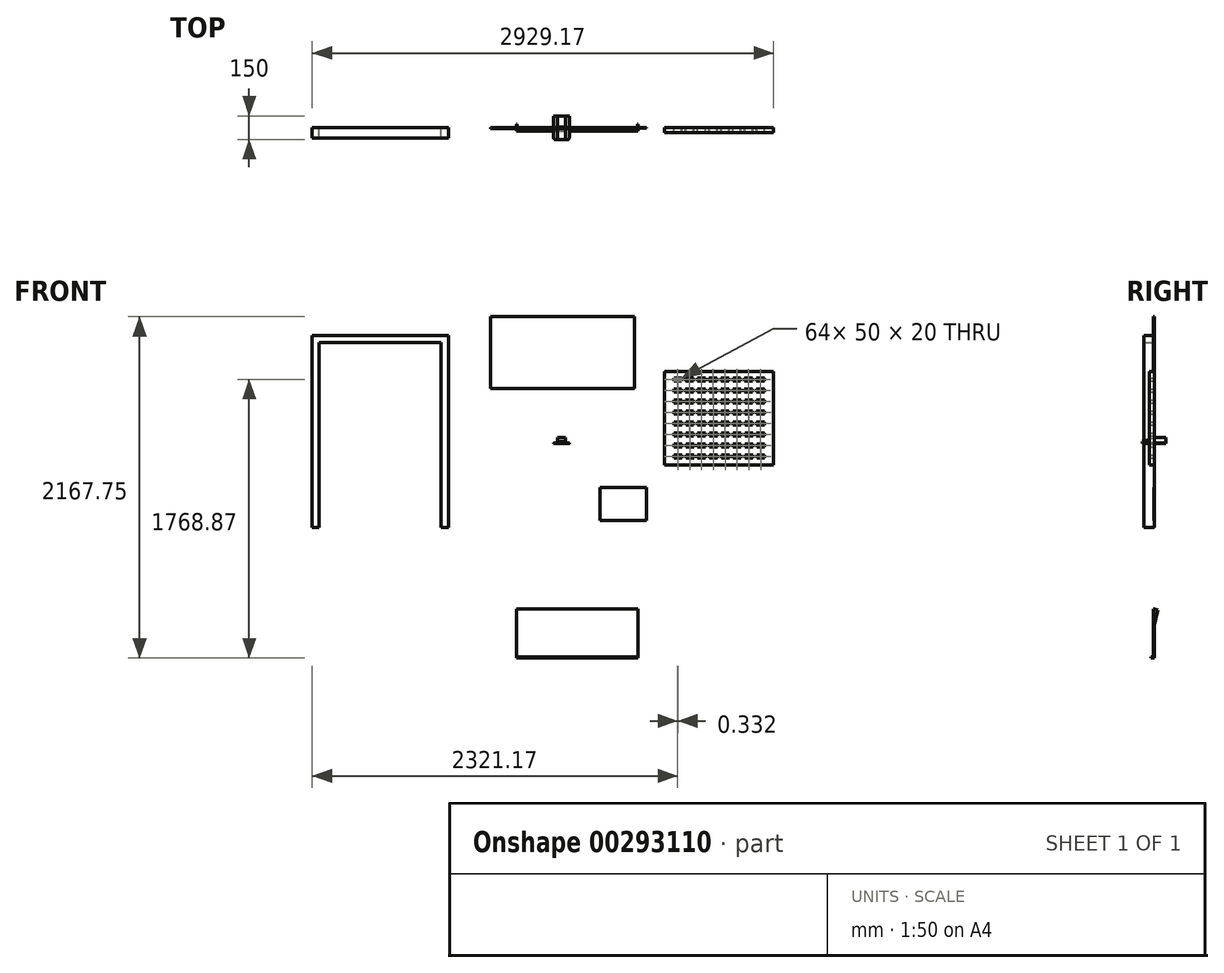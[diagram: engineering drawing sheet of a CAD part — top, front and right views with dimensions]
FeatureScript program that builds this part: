
annotation { "Feature Type Name" : "Feature", "Feature Type Description" : "" }
export const myFeature = defineFeature(function(context is Context, id is Id, definition is map)
    precondition{}
    {
        {
            var Q0;
            Q0=qCreatedBy(makeId("Top.planeOp"),FACE);
            var sketch = newSketch(context, id + "F0", { "sketchPlane" : qUnion([Q0])});
            skLineSegment(sketch, "E0.bottom", {"start": v(-50, 75) * mm, "end": v(50, 75) * mm});
            skLineSegment(sketch, "E0.top", {"start": v(-50, -75) * mm, "end": v(50, -75) * mm});
            skLineSegment(sketch, "E0.left", {"start": v(-50, 75) * mm, "end": v(-50, -75) * mm});
            skLineSegment(sketch, "E0.right", {"start": v(50, 75) * mm, "end": v(50, -75) * mm});
            skPoint(sketch, "E0.middle", {"position": v(0, 0) * mm});
            skSolve(sketch);
        }
        {
            var Q0;
            Q0=makeQuery(id+"F0.imprint","IMPRINT",FACE,{"disambiguationData":[TD([[makeQuery(id+"F0.imprint","IMPRINT",EDGE,{"derivedFrom":sQuery(id+"F0.wireOp",EDGE,"E0.bottom")}),-1.0]])]});
            extrude(context, id + "F1", {"entities" : qUnion([Q0]), "depth" : 3 * mm});
        }
        {
            var Q0;
            Q0=makeQuery(id+"F1.opExtrude","SWEPT_EDGE",EDGE,{"disambiguationData":[OSD([sQuery(id+"F0.wireOp",EDGE,"E0.top"),sQuery(id+"F0.wireOp",EDGE,"E0.left")])]});
            var Q1;
            Q1=makeQuery(id+"F1.opExtrude","SWEPT_EDGE",EDGE,{"disambiguationData":[OSD([sQuery(id+"F0.wireOp",EDGE,"E0.top"),sQuery(id+"F0.wireOp",EDGE,"E0.right")])]});
            fillet(context, id + "F2", {"entities" : qUnion([Q0, Q1]), "radius" : 10 * mm, "tangentPropagation" : true, "allowEdgeOverflow" : false});
        }
        {
            var Q0;
            Q0=makeQuery(id+"F1.opExtrude","CAP_FACE",FACE,{"disambiguationData":[OSD([sQuery(id+"F0.wireOp",EDGE,"E0.bottom"),sQuery(id+"F0.wireOp",EDGE,"E0.top"),sQuery(id+"F0.wireOp",EDGE,"E0.left"),sQuery(id+"F0.wireOp",EDGE,"E0.right")])],"isStart":false});
            var sketch = newSketch(context, id + "F3", { "sketchPlane" : qUnion([Q0])});
            skLineSegment(sketch, "E1.bottom", {"start": v(-25, 75) * mm, "end": v(25, 75) * mm});
            skLineSegment(sketch, "E1.top", {"start": v(-25, -75) * mm, "end": v(25, -75) * mm});
            skLineSegment(sketch, "E1.left", {"start": v(-25, 75) * mm, "end": v(-25, -75) * mm});
            skLineSegment(sketch, "E1.right", {"start": v(25, 75) * mm, "end": v(25, -75) * mm});
            skPoint(sketch, "E1.middle", {"position": v(0, 0) * mm});
            skSolve(sketch);
        }
        {
            var Q0;
            {var subQ0=sQuery(id+"F3.wireOp",EDGE,"E1.bottom");Q0=makeQuery(id+"F3.imprint","IMPRINT",FACE,{"disambiguationData":[TD([[makeQuery(id+"F3.imprint","IMPRINT",EDGE,{"derivedFrom":subQ0}),-1.0]])]});}
            extrude(context, id + "F4", {"entities" : qUnion([Q0]), "operationType" : NewBodyOperationType.ADD, "depth" : 35 * mm});
        }
        {
            var Q0;
            Q0=makeQuery(id+"F4.opExtrude","SWEPT_FACE",FACE,{"disambiguationData":[OSD([sQuery(id+"F3.wireOp",EDGE,"E1.right")])]});
            var sketch = newSketch(context, id + "F5", { "sketchPlane" : qUnion([Q0])});
            skLineSegment(sketch, "E2", {"start": v(5, 3) * mm, "end": v(5, 38) * mm});
            skLineSegment(sketch, "E3", {"start": v(5, 38) * mm, "end": v(-75, 13) * mm});
            skLineSegment(sketch, "E4", {"start": v(-75, 13) * mm, "end": v(-75, 3) * mm});
            skLineSegment(sketch, "E5", {"start": v(-75, 3) * mm, "end": v(5, 3) * mm});
            skSolve(sketch);
        }
        {
            var Q0;
            {var subQ0=sQuery(id+"F5.wireOp",EDGE,"E3");Q0=makeQuery(id+"F5.imprint","IMPRINT",FACE,{"disambiguationData":[TD([[makeQuery(id+"F5.imprint","IMPRINT",EDGE,{"derivedFrom":subQ0}),-1.0]])]});}
            extrude(context, id + "F6", {"entities" : qUnion([Q0]), "operationType" : NewBodyOperationType.REMOVE, "endBound" : BoundingType.THROUGH_ALL, "oppositeDirection" : true, "depth" : 25 * mm});
        }
        {
            var Q0;
            Q0=qCreatedBy(makeId("Front.planeOp"),FACE);
            var sketch = newSketch(context, id + "F7", { "sketchPlane" : qUnion([Q0])});
            skLineSegment(sketch, "E6.bottom", {"start": v(-1582.46, -533.96) * mm, "end": v(-1537.46, -533.96) * mm});
            skLineSegment(sketch, "E6.left", {"start": v(-1582.46, -533.96) * mm, "end": v(-1582.46, 685.04) * mm});
            skLineSegment(sketch, "E6.right", {"start": v(-1537.46, -533.96) * mm, "end": v(-1537.46, 640.04) * mm});
            skLineSegment(sketch, "E7.top", {"start": v(-1537.46, 640.04) * mm, "end": v(-763.06, 640.04) * mm});
            skLineSegment(sketch, "E8.top", {"start": v(-763.06, -533.96) * mm, "end": v(-718.06, -533.96) * mm});
            skLineSegment(sketch, "E8.left", {"start": v(-763.06, 640.04) * mm, "end": v(-763.06, -533.96) * mm});
            skLineSegment(sketch, "E8.right", {"start": v(-718.06, 685.04) * mm, "end": v(-718.06, -533.96) * mm});
            skLineSegment(sketch, "E9", {"start": v(-1582.46, 685.04) * mm, "end": v(-718.06, 685.04) * mm});
            skSolve(sketch);
        }
        {
            var Q0;
            {var subQ0=sQuery(id+"F7.wireOp",EDGE,"E7.bottom");Q0=makeQuery(id+"F7.imprint","IMPRINT",FACE,{"disambiguationData":[TD([[makeQuery(id+"F7.imprint","IMPRINT",EDGE,{"derivedFrom":subQ0}),-1.0]])]});}
            var Q1;
            Q1=makeQuery(id+"F7.imprint","IMPRINT",FACE,{"disambiguationData":[TD([[makeQuery(id+"F7.imprint","IMPRINT",EDGE,{"derivedFrom":sQuery(id+"F7.wireOp",EDGE,"E6.bottom")}),1.0]])]});
            var Q2;
            {var subQ3=sQuery(id+"F7.wireOp",EDGE,"Cl1eL8Ux-WlNg-qc7l-GYTB-HFergLuJIKgZ.bottom");Q2=makeQuery(id+"F7.imprint","IMPRINT",FACE,{"disambiguationData":[TD([[makeQuery(id+"F7.imprint","IMPRINT",EDGE,{"derivedFrom":subQ3}),-1.0]])]});}
            var Q3;
            {var subQ0=sQuery(id+"F7.wireOp",EDGE,"AxVRE3I6-bPMa-kPDy-dnkS-AJJv6BN4a7yn.bottom");Q3=makeQuery(id+"F7.imprint","IMPRINT",FACE,{"disambiguationData":[TD([[makeQuery(id+"F7.imprint","IMPRINT",EDGE,{"derivedFrom":subQ0}),-1.0]])]});}
            var Q4;
            {var subQ3=sQuery(id+"F7.wireOp",EDGE,"E8.bottom");Q4=makeQuery(id+"F7.imprint","IMPRINT",FACE,{"disambiguationData":[TD([[makeQuery(id+"F7.imprint","IMPRINT",EDGE,{"derivedFrom":subQ3}),-1.0]])]});}
            extrude(context, id + "F8", {"entities" : qUnion([Q0, Q1, Q2, Q3, Q4]), "depth" : 65 * mm});
        }
        {
            var Q0;
            Q0=qCreatedBy(makeId("Front.planeOp"),FACE);
            var sketch = newSketch(context, id + "F9", { "sketchPlane" : qUnion([Q0])});
            skLineSegment(sketch, "E10.bottom", {"start": v(653.71, 457) * mm, "end": v(1346.71, 457) * mm});
            skLineSegment(sketch, "E10.top", {"start": v(653.71, -136) * mm, "end": v(1346.71, -136) * mm});
            skLineSegment(sketch, "E10.left", {"start": v(653.71, 457) * mm, "end": v(653.71, -136) * mm});
            skLineSegment(sketch, "E10.right", {"start": v(1346.71, 457) * mm, "end": v(1346.71, -136) * mm});
            skLineSegment(sketch, "E11.bottom", {"start": v(713.71, 417) * mm, "end": v(763.71, 417) * mm});
            skLineSegment(sketch, "E11.top", {"start": v(713.71, 397) * mm, "end": v(763.71, 397) * mm});
            skLineSegment(sketch, "E11.left", {"start": v(713.71, 417) * mm, "end": v(713.71, 397) * mm});
            skLineSegment(sketch, "E11.right", {"start": v(763.71, 417) * mm, "end": v(763.71, 397) * mm});
            skLineSegment(sketch, "E12.0.1.0", {"start": v(714.04, 347) * mm, "end": v(764.04, 347) * mm});
            skLineSegment(sketch, "E12.0.1.1", {"start": v(714.04, 327) * mm, "end": v(764.04, 327) * mm});
            skLineSegment(sketch, "E12.0.1.2", {"start": v(714.04, 347) * mm, "end": v(714.04, 327) * mm});
            skLineSegment(sketch, "E12.0.2.0", {"start": v(714.37, 277) * mm, "end": v(764.37, 277) * mm});
            skLineSegment(sketch, "E12.0.2.1", {"start": v(714.37, 257) * mm, "end": v(764.37, 257) * mm});
            skLineSegment(sketch, "E12.0.2.2", {"start": v(714.37, 277) * mm, "end": v(714.37, 257) * mm});
            skLineSegment(sketch, "E12.0.3.0", {"start": v(714.7, 207) * mm, "end": v(764.7, 207) * mm});
            skLineSegment(sketch, "E12.0.3.1", {"start": v(714.7, 187) * mm, "end": v(764.7, 187) * mm});
            skLineSegment(sketch, "E12.0.3.2", {"start": v(714.7, 207) * mm, "end": v(714.7, 187) * mm});
            skLineSegment(sketch, "E12.0.4.0", {"start": v(715.04, 137) * mm, "end": v(765.04, 137) * mm});
            skLineSegment(sketch, "E12.0.4.1", {"start": v(715.04, 117) * mm, "end": v(765.04, 117) * mm});
            skLineSegment(sketch, "E12.0.4.2", {"start": v(715.04, 137) * mm, "end": v(715.04, 117) * mm});
            skLineSegment(sketch, "E12.0.5.0", {"start": v(715.37, 67) * mm, "end": v(765.37, 67) * mm});
            skLineSegment(sketch, "E12.0.5.1", {"start": v(715.37, 47) * mm, "end": v(765.37, 47) * mm});
            skLineSegment(sketch, "E12.0.5.2", {"start": v(715.37, 67) * mm, "end": v(715.37, 47) * mm});
            skLineSegment(sketch, "E12.0.6.0", {"start": v(715.7, -3) * mm, "end": v(765.7, -3) * mm});
            skLineSegment(sketch, "E12.0.6.1", {"start": v(715.7, -23) * mm, "end": v(765.7, -23) * mm});
            skLineSegment(sketch, "E12.0.6.2", {"start": v(715.7, -3) * mm, "end": v(715.7, -23) * mm});
            skLineSegment(sketch, "E12.1.0.0", {"start": v(788.71, 417) * mm, "end": v(838.71, 417) * mm});
            skLineSegment(sketch, "E12.1.0.1", {"start": v(788.71, 397) * mm, "end": v(838.71, 397) * mm});
            skLineSegment(sketch, "E12.1.0.2", {"start": v(788.71, 417) * mm, "end": v(788.71, 397) * mm});
            skLineSegment(sketch, "E12.1.1.0", {"start": v(789.04, 347) * mm, "end": v(839.04, 347) * mm});
            skLineSegment(sketch, "E12.1.1.1", {"start": v(789.04, 327) * mm, "end": v(839.04, 327) * mm});
            skLineSegment(sketch, "E12.1.1.2", {"start": v(789.04, 347) * mm, "end": v(789.04, 327) * mm});
            skLineSegment(sketch, "E12.1.2.0", {"start": v(789.37, 277) * mm, "end": v(839.37, 277) * mm});
            skLineSegment(sketch, "E12.1.2.1", {"start": v(789.37, 257) * mm, "end": v(839.37, 257) * mm});
            skLineSegment(sketch, "E12.1.2.2", {"start": v(789.37, 277) * mm, "end": v(789.37, 257) * mm});
            skLineSegment(sketch, "E12.1.3.0", {"start": v(789.7, 207) * mm, "end": v(839.7, 207) * mm});
            skLineSegment(sketch, "E12.1.3.1", {"start": v(789.7, 187) * mm, "end": v(839.7, 187) * mm});
            skLineSegment(sketch, "E12.1.3.2", {"start": v(789.7, 207) * mm, "end": v(789.7, 187) * mm});
            skLineSegment(sketch, "E12.1.4.0", {"start": v(790.04, 137) * mm, "end": v(840.04, 137) * mm});
            skLineSegment(sketch, "E12.1.4.1", {"start": v(790.04, 117) * mm, "end": v(840.04, 117) * mm});
            skLineSegment(sketch, "E12.1.4.2", {"start": v(790.04, 137) * mm, "end": v(790.04, 117) * mm});
            skLineSegment(sketch, "E12.1.5.0", {"start": v(790.37, 67) * mm, "end": v(840.37, 67) * mm});
            skLineSegment(sketch, "E12.1.5.1", {"start": v(790.37, 47) * mm, "end": v(840.37, 47) * mm});
            skLineSegment(sketch, "E12.1.5.2", {"start": v(790.37, 67) * mm, "end": v(790.37, 47) * mm});
            skLineSegment(sketch, "E12.1.6.0", {"start": v(790.7, -3) * mm, "end": v(840.7, -3) * mm});
            skLineSegment(sketch, "E12.1.6.1", {"start": v(790.7, -23) * mm, "end": v(840.7, -23) * mm});
            skLineSegment(sketch, "E12.1.6.2", {"start": v(790.7, -3) * mm, "end": v(790.7, -23) * mm});
            skLineSegment(sketch, "E12.2.0.0", {"start": v(863.71, 417) * mm, "end": v(913.71, 417) * mm});
            skLineSegment(sketch, "E12.2.0.1", {"start": v(863.71, 397) * mm, "end": v(913.71, 397) * mm});
            skLineSegment(sketch, "E12.2.0.2", {"start": v(863.71, 417) * mm, "end": v(863.71, 397) * mm});
            skLineSegment(sketch, "E12.2.1.0", {"start": v(864.04, 347) * mm, "end": v(914.04, 347) * mm});
            skLineSegment(sketch, "E12.2.1.1", {"start": v(864.04, 327) * mm, "end": v(914.04, 327) * mm});
            skLineSegment(sketch, "E12.2.1.2", {"start": v(864.04, 347) * mm, "end": v(864.04, 327) * mm});
            skLineSegment(sketch, "E12.2.2.0", {"start": v(864.37, 277) * mm, "end": v(914.37, 277) * mm});
            skLineSegment(sketch, "E12.2.2.1", {"start": v(864.37, 257) * mm, "end": v(914.37, 257) * mm});
            skLineSegment(sketch, "E12.2.2.2", {"start": v(864.37, 277) * mm, "end": v(864.37, 257) * mm});
            skLineSegment(sketch, "E12.2.3.0", {"start": v(864.7, 207) * mm, "end": v(914.7, 207) * mm});
            skLineSegment(sketch, "E12.2.3.1", {"start": v(864.7, 187) * mm, "end": v(914.7, 187) * mm});
            skLineSegment(sketch, "E12.2.3.2", {"start": v(864.7, 207) * mm, "end": v(864.7, 187) * mm});
            skLineSegment(sketch, "E12.2.4.0", {"start": v(865.04, 137) * mm, "end": v(915.04, 137) * mm});
            skLineSegment(sketch, "E12.2.4.1", {"start": v(865.04, 117) * mm, "end": v(915.04, 117) * mm});
            skLineSegment(sketch, "E12.2.4.2", {"start": v(865.04, 137) * mm, "end": v(865.04, 117) * mm});
            skLineSegment(sketch, "E12.2.5.0", {"start": v(865.37, 67) * mm, "end": v(915.37, 67) * mm});
            skLineSegment(sketch, "E12.2.5.1", {"start": v(865.37, 47) * mm, "end": v(915.37, 47) * mm});
            skLineSegment(sketch, "E12.2.5.2", {"start": v(865.37, 67) * mm, "end": v(865.37, 47) * mm});
            skLineSegment(sketch, "E12.2.6.0", {"start": v(865.7, -3) * mm, "end": v(915.7, -3) * mm});
            skLineSegment(sketch, "E12.2.6.1", {"start": v(865.7, -23) * mm, "end": v(915.7, -23) * mm});
            skLineSegment(sketch, "E12.2.6.2", {"start": v(865.7, -3) * mm, "end": v(865.7, -23) * mm});
            skLineSegment(sketch, "E12.3.0.0", {"start": v(938.71, 417) * mm, "end": v(988.71, 417) * mm});
            skLineSegment(sketch, "E12.3.0.1", {"start": v(938.71, 397) * mm, "end": v(988.71, 397) * mm});
            skLineSegment(sketch, "E12.3.0.2", {"start": v(938.71, 417) * mm, "end": v(938.71, 397) * mm});
            skLineSegment(sketch, "E12.3.1.0", {"start": v(939.04, 347) * mm, "end": v(989.04, 347) * mm});
            skLineSegment(sketch, "E12.3.1.1", {"start": v(939.04, 327) * mm, "end": v(989.04, 327) * mm});
            skLineSegment(sketch, "E12.3.1.2", {"start": v(939.04, 347) * mm, "end": v(939.04, 327) * mm});
            skLineSegment(sketch, "E12.3.2.0", {"start": v(939.37, 277) * mm, "end": v(989.37, 277) * mm});
            skLineSegment(sketch, "E12.3.2.1", {"start": v(939.37, 257) * mm, "end": v(989.37, 257) * mm});
            skLineSegment(sketch, "E12.3.2.2", {"start": v(939.37, 277) * mm, "end": v(939.37, 257) * mm});
            skLineSegment(sketch, "E12.3.3.0", {"start": v(939.7, 207) * mm, "end": v(989.7, 207) * mm});
            skLineSegment(sketch, "E12.3.3.1", {"start": v(939.7, 187) * mm, "end": v(989.7, 187) * mm});
            skLineSegment(sketch, "E12.3.3.2", {"start": v(939.7, 207) * mm, "end": v(939.7, 187) * mm});
            skLineSegment(sketch, "E12.3.4.0", {"start": v(940.04, 137) * mm, "end": v(990.04, 137) * mm});
            skLineSegment(sketch, "E12.3.4.1", {"start": v(940.04, 117) * mm, "end": v(990.04, 117) * mm});
            skLineSegment(sketch, "E12.3.4.2", {"start": v(940.04, 137) * mm, "end": v(940.04, 117) * mm});
            skLineSegment(sketch, "E12.3.5.0", {"start": v(940.37, 67) * mm, "end": v(990.37, 67) * mm});
            skLineSegment(sketch, "E12.3.5.1", {"start": v(940.37, 47) * mm, "end": v(990.37, 47) * mm});
            skLineSegment(sketch, "E12.3.5.2", {"start": v(940.37, 67) * mm, "end": v(940.37, 47) * mm});
            skLineSegment(sketch, "E12.3.6.0", {"start": v(940.7, -3) * mm, "end": v(990.7, -3) * mm});
            skLineSegment(sketch, "E12.3.6.1", {"start": v(940.7, -23) * mm, "end": v(990.7, -23) * mm});
            skLineSegment(sketch, "E12.3.6.2", {"start": v(940.7, -3) * mm, "end": v(940.7, -23) * mm});
            skLineSegment(sketch, "E12.4.0.0", {"start": v(1013.71, 417) * mm, "end": v(1063.71, 417) * mm});
            skLineSegment(sketch, "E12.4.0.1", {"start": v(1013.71, 397) * mm, "end": v(1063.71, 397) * mm});
            skLineSegment(sketch, "E12.4.0.2", {"start": v(1013.71, 417) * mm, "end": v(1013.71, 397) * mm});
            skLineSegment(sketch, "E12.4.1.0", {"start": v(1014.04, 347) * mm, "end": v(1064.04, 347) * mm});
            skLineSegment(sketch, "E12.4.1.1", {"start": v(1014.04, 327) * mm, "end": v(1064.04, 327) * mm});
            skLineSegment(sketch, "E12.4.1.2", {"start": v(1014.04, 347) * mm, "end": v(1014.04, 327) * mm});
            skLineSegment(sketch, "E12.4.2.0", {"start": v(1014.37, 277) * mm, "end": v(1064.37, 277) * mm});
            skLineSegment(sketch, "E12.4.2.1", {"start": v(1014.37, 257) * mm, "end": v(1064.37, 257) * mm});
            skLineSegment(sketch, "E12.4.2.2", {"start": v(1014.37, 277) * mm, "end": v(1014.37, 257) * mm});
            skLineSegment(sketch, "E12.4.3.0", {"start": v(1014.7, 207) * mm, "end": v(1064.7, 207) * mm});
            skLineSegment(sketch, "E12.4.3.1", {"start": v(1014.7, 187) * mm, "end": v(1064.7, 187) * mm});
            skLineSegment(sketch, "E12.4.3.2", {"start": v(1014.7, 207) * mm, "end": v(1014.7, 187) * mm});
            skLineSegment(sketch, "E12.4.4.0", {"start": v(1015.04, 137) * mm, "end": v(1065.04, 137) * mm});
            skLineSegment(sketch, "E12.4.4.1", {"start": v(1015.04, 117) * mm, "end": v(1065.04, 117) * mm});
            skLineSegment(sketch, "E12.4.4.2", {"start": v(1015.04, 137) * mm, "end": v(1015.04, 117) * mm});
            skLineSegment(sketch, "E12.4.5.0", {"start": v(1015.37, 67) * mm, "end": v(1065.37, 67) * mm});
            skLineSegment(sketch, "E12.4.5.1", {"start": v(1015.37, 47) * mm, "end": v(1065.37, 47) * mm});
            skLineSegment(sketch, "E12.4.5.2", {"start": v(1015.37, 67) * mm, "end": v(1015.37, 47) * mm});
            skLineSegment(sketch, "E12.4.6.0", {"start": v(1015.7, -3) * mm, "end": v(1065.7, -3) * mm});
            skLineSegment(sketch, "E12.4.6.1", {"start": v(1015.7, -23) * mm, "end": v(1065.7, -23) * mm});
            skLineSegment(sketch, "E12.4.6.2", {"start": v(1015.7, -3) * mm, "end": v(1015.7, -23) * mm});
            skLineSegment(sketch, "E12.5.0.0", {"start": v(1088.71, 417) * mm, "end": v(1138.71, 417) * mm});
            skLineSegment(sketch, "E12.5.0.1", {"start": v(1088.71, 397) * mm, "end": v(1138.71, 397) * mm});
            skLineSegment(sketch, "E12.5.0.2", {"start": v(1088.71, 417) * mm, "end": v(1088.71, 397) * mm});
            skLineSegment(sketch, "E12.5.1.0", {"start": v(1089.04, 347) * mm, "end": v(1139.04, 347) * mm});
            skLineSegment(sketch, "E12.5.1.1", {"start": v(1089.04, 327) * mm, "end": v(1139.04, 327) * mm});
            skLineSegment(sketch, "E12.5.1.2", {"start": v(1089.04, 347) * mm, "end": v(1089.04, 327) * mm});
            skLineSegment(sketch, "E12.5.2.0", {"start": v(1089.37, 277) * mm, "end": v(1139.37, 277) * mm});
            skLineSegment(sketch, "E12.5.2.1", {"start": v(1089.37, 257) * mm, "end": v(1139.37, 257) * mm});
            skLineSegment(sketch, "E12.5.2.2", {"start": v(1089.37, 277) * mm, "end": v(1089.37, 257) * mm});
            skLineSegment(sketch, "E12.5.3.0", {"start": v(1089.7, 207) * mm, "end": v(1139.7, 207) * mm});
            skLineSegment(sketch, "E12.5.3.1", {"start": v(1089.7, 187) * mm, "end": v(1139.7, 187) * mm});
            skLineSegment(sketch, "E12.5.3.2", {"start": v(1089.7, 207) * mm, "end": v(1089.7, 187) * mm});
            skLineSegment(sketch, "E12.5.4.0", {"start": v(1090.04, 137) * mm, "end": v(1140.04, 137) * mm});
            skLineSegment(sketch, "E12.5.4.1", {"start": v(1090.04, 117) * mm, "end": v(1140.04, 117) * mm});
            skLineSegment(sketch, "E12.5.4.2", {"start": v(1090.04, 137) * mm, "end": v(1090.04, 117) * mm});
            skLineSegment(sketch, "E12.5.5.0", {"start": v(1090.37, 67) * mm, "end": v(1140.37, 67) * mm});
            skLineSegment(sketch, "E12.5.5.1", {"start": v(1090.37, 47) * mm, "end": v(1140.37, 47) * mm});
            skLineSegment(sketch, "E12.5.5.2", {"start": v(1090.37, 67) * mm, "end": v(1090.37, 47) * mm});
            skLineSegment(sketch, "E12.5.6.0", {"start": v(1090.7, -3) * mm, "end": v(1140.7, -3) * mm});
            skLineSegment(sketch, "E12.5.6.1", {"start": v(1090.7, -23) * mm, "end": v(1140.7, -23) * mm});
            skLineSegment(sketch, "E12.5.6.2", {"start": v(1090.7, -3) * mm, "end": v(1090.7, -23) * mm});
            skLineSegment(sketch, "E12.6.0.0", {"start": v(1163.71, 417) * mm, "end": v(1213.71, 417) * mm});
            skLineSegment(sketch, "E12.6.0.1", {"start": v(1163.71, 397) * mm, "end": v(1213.71, 397) * mm});
            skLineSegment(sketch, "E12.6.0.2", {"start": v(1163.71, 417) * mm, "end": v(1163.71, 397) * mm});
            skLineSegment(sketch, "E12.6.1.0", {"start": v(1164.04, 347) * mm, "end": v(1214.04, 347) * mm});
            skLineSegment(sketch, "E12.6.1.1", {"start": v(1164.04, 327) * mm, "end": v(1214.04, 327) * mm});
            skLineSegment(sketch, "E12.6.1.2", {"start": v(1164.04, 347) * mm, "end": v(1164.04, 327) * mm});
            skLineSegment(sketch, "E12.6.2.0", {"start": v(1164.37, 277) * mm, "end": v(1214.37, 277) * mm});
            skLineSegment(sketch, "E12.6.2.1", {"start": v(1164.37, 257) * mm, "end": v(1214.37, 257) * mm});
            skLineSegment(sketch, "E12.6.2.2", {"start": v(1164.37, 277) * mm, "end": v(1164.37, 257) * mm});
            skLineSegment(sketch, "E12.6.3.0", {"start": v(1164.7, 207) * mm, "end": v(1214.7, 207) * mm});
            skLineSegment(sketch, "E12.6.3.1", {"start": v(1164.7, 187) * mm, "end": v(1214.7, 187) * mm});
            skLineSegment(sketch, "E12.6.3.2", {"start": v(1164.7, 207) * mm, "end": v(1164.7, 187) * mm});
            skLineSegment(sketch, "E12.6.4.0", {"start": v(1165.04, 137) * mm, "end": v(1215.04, 137) * mm});
            skLineSegment(sketch, "E12.6.4.1", {"start": v(1165.04, 117) * mm, "end": v(1215.04, 117) * mm});
            skLineSegment(sketch, "E12.6.4.2", {"start": v(1165.04, 137) * mm, "end": v(1165.04, 117) * mm});
            skLineSegment(sketch, "E12.6.5.0", {"start": v(1165.37, 67) * mm, "end": v(1215.37, 67) * mm});
            skLineSegment(sketch, "E12.6.5.1", {"start": v(1165.37, 47) * mm, "end": v(1215.37, 47) * mm});
            skLineSegment(sketch, "E12.6.5.2", {"start": v(1165.37, 67) * mm, "end": v(1165.37, 47) * mm});
            skLineSegment(sketch, "E12.6.6.0", {"start": v(1165.7, -3) * mm, "end": v(1215.7, -3) * mm});
            skLineSegment(sketch, "E12.6.6.1", {"start": v(1165.7, -23) * mm, "end": v(1215.7, -23) * mm});
            skLineSegment(sketch, "E12.6.6.2", {"start": v(1165.7, -3) * mm, "end": v(1165.7, -23) * mm});
            skLineSegment(sketch, "E12.7.0.0", {"start": v(1238.71, 417) * mm, "end": v(1288.71, 417) * mm});
            skLineSegment(sketch, "E12.7.0.1", {"start": v(1238.71, 397) * mm, "end": v(1288.71, 397) * mm});
            skLineSegment(sketch, "E12.7.0.2", {"start": v(1238.71, 417) * mm, "end": v(1238.71, 397) * mm});
            skLineSegment(sketch, "E12.7.1.0", {"start": v(1239.04, 347) * mm, "end": v(1289.04, 347) * mm});
            skLineSegment(sketch, "E12.7.1.1", {"start": v(1239.04, 327) * mm, "end": v(1289.04, 327) * mm});
            skLineSegment(sketch, "E12.7.1.2", {"start": v(1239.04, 347) * mm, "end": v(1239.04, 327) * mm});
            skLineSegment(sketch, "E12.7.2.0", {"start": v(1239.37, 277) * mm, "end": v(1289.37, 277) * mm});
            skLineSegment(sketch, "E12.7.2.1", {"start": v(1239.37, 257) * mm, "end": v(1289.37, 257) * mm});
            skLineSegment(sketch, "E12.7.2.2", {"start": v(1239.37, 277) * mm, "end": v(1239.37, 257) * mm});
            skLineSegment(sketch, "E12.7.3.0", {"start": v(1239.7, 207) * mm, "end": v(1289.7, 207) * mm});
            skLineSegment(sketch, "E12.7.3.1", {"start": v(1239.7, 187) * mm, "end": v(1289.7, 187) * mm});
            skLineSegment(sketch, "E12.7.3.2", {"start": v(1239.7, 207) * mm, "end": v(1239.7, 187) * mm});
            skLineSegment(sketch, "E12.7.4.0", {"start": v(1240.04, 137) * mm, "end": v(1290.04, 137) * mm});
            skLineSegment(sketch, "E12.7.4.1", {"start": v(1240.04, 117) * mm, "end": v(1290.04, 117) * mm});
            skLineSegment(sketch, "E12.7.4.2", {"start": v(1240.04, 137) * mm, "end": v(1240.04, 117) * mm});
            skLineSegment(sketch, "E12.7.5.0", {"start": v(1240.37, 67) * mm, "end": v(1290.37, 67) * mm});
            skLineSegment(sketch, "E12.7.5.1", {"start": v(1240.37, 47) * mm, "end": v(1290.37, 47) * mm});
            skLineSegment(sketch, "E12.7.5.2", {"start": v(1240.37, 67) * mm, "end": v(1240.37, 47) * mm});
            skLineSegment(sketch, "E12.7.6.0", {"start": v(1240.7, -3) * mm, "end": v(1290.7, -3) * mm});
            skLineSegment(sketch, "E12.7.6.1", {"start": v(1240.7, -23) * mm, "end": v(1290.7, -23) * mm});
            skLineSegment(sketch, "E12.7.6.2", {"start": v(1240.7, -3) * mm, "end": v(1240.7, -23) * mm});
            skLineSegment(sketch, "E12.direction1", {"start": v(713.71, 417) * mm, "end": v(788.71, 417) * mm, "construction": true});
            skLineSegment(sketch, "E12.direction2", {"start": v(713.71, 417) * mm, "end": v(714.04, 347) * mm, "construction": true});
            skLineSegment(sketch, "E13.0.0.7", {"start": v(716.03, -73) * mm, "end": v(766.03, -73) * mm});
            skLineSegment(sketch, "E13.3.0.7", {"start": v(716.03, -93) * mm, "end": v(766.03, -93) * mm});
            skLineSegment(sketch, "E13.6.0.7", {"start": v(716.03, -73) * mm, "end": v(716.03, -93) * mm});
            skLineSegment(sketch, "E13.0.1.7", {"start": v(791.03, -73) * mm, "end": v(841.03, -73) * mm});
            skLineSegment(sketch, "E13.3.1.7", {"start": v(791.03, -93) * mm, "end": v(841.03, -93) * mm});
            skLineSegment(sketch, "E13.6.1.7", {"start": v(791.03, -73) * mm, "end": v(791.03, -93) * mm});
            skLineSegment(sketch, "E13.0.2.7", {"start": v(866.03, -73) * mm, "end": v(916.03, -73) * mm});
            skLineSegment(sketch, "E13.3.2.7", {"start": v(866.03, -93) * mm, "end": v(916.03, -93) * mm});
            skLineSegment(sketch, "E13.6.2.7", {"start": v(866.03, -73) * mm, "end": v(866.03, -93) * mm});
            skLineSegment(sketch, "E13.0.3.7", {"start": v(941.03, -73) * mm, "end": v(991.03, -73) * mm});
            skLineSegment(sketch, "E13.3.3.7", {"start": v(941.03, -93) * mm, "end": v(991.03, -93) * mm});
            skLineSegment(sketch, "E13.6.3.7", {"start": v(941.03, -73) * mm, "end": v(941.03, -93) * mm});
            skLineSegment(sketch, "E13.0.4.7", {"start": v(1016.03, -73) * mm, "end": v(1066.03, -73) * mm});
            skLineSegment(sketch, "E13.3.4.7", {"start": v(1016.03, -93) * mm, "end": v(1066.03, -93) * mm});
            skLineSegment(sketch, "E13.6.4.7", {"start": v(1016.03, -73) * mm, "end": v(1016.03, -93) * mm});
            skLineSegment(sketch, "E13.0.5.7", {"start": v(1091.03, -73) * mm, "end": v(1141.03, -73) * mm});
            skLineSegment(sketch, "E13.3.5.7", {"start": v(1091.03, -93) * mm, "end": v(1141.03, -93) * mm});
            skLineSegment(sketch, "E13.6.5.7", {"start": v(1091.03, -73) * mm, "end": v(1091.03, -93) * mm});
            skLineSegment(sketch, "E13.0.6.7", {"start": v(1166.03, -73) * mm, "end": v(1216.03, -73) * mm});
            skLineSegment(sketch, "E13.3.6.7", {"start": v(1166.03, -93) * mm, "end": v(1216.03, -93) * mm});
            skLineSegment(sketch, "E13.6.6.7", {"start": v(1166.03, -73) * mm, "end": v(1166.03, -93) * mm});
            skLineSegment(sketch, "E13.0.7.7", {"start": v(1241.03, -73) * mm, "end": v(1291.03, -73) * mm});
            skLineSegment(sketch, "E13.3.7.7", {"start": v(1241.03, -93) * mm, "end": v(1291.03, -93) * mm});
            skLineSegment(sketch, "E13.6.7.7", {"start": v(1241.03, -73) * mm, "end": v(1241.03, -93) * mm});
            skLineSegment(sketch, "E14", {"start": v(838.71, 417) * mm, "end": v(838.71, 397) * mm});
            skLineSegment(sketch, "E15", {"start": v(913.71, 417) * mm, "end": v(913.71, 397) * mm});
            skLineSegment(sketch, "E16", {"start": v(988.71, 417) * mm, "end": v(988.71, 397) * mm});
            skLineSegment(sketch, "E17", {"start": v(1063.71, 417) * mm, "end": v(1063.71, 397) * mm});
            skLineSegment(sketch, "E18", {"start": v(1138.71, 417) * mm, "end": v(1138.71, 397) * mm});
            skLineSegment(sketch, "E19", {"start": v(1213.71, 417) * mm, "end": v(1213.71, 397) * mm});
            skLineSegment(sketch, "E20", {"start": v(1288.71, 417) * mm, "end": v(1288.71, 397) * mm});
            skLineSegment(sketch, "E21", {"start": v(1289.04, 347) * mm, "end": v(1289.04, 327) * mm});
            skLineSegment(sketch, "E22", {"start": v(1214.04, 347) * mm, "end": v(1214.04, 327) * mm});
            skLineSegment(sketch, "E23", {"start": v(1139.04, 347) * mm, "end": v(1139.04, 327) * mm});
            skLineSegment(sketch, "E24", {"start": v(1064.04, 347) * mm, "end": v(1064.04, 327) * mm});
            skLineSegment(sketch, "E25", {"start": v(989.04, 347) * mm, "end": v(989.04, 327) * mm});
            skLineSegment(sketch, "E26", {"start": v(914.04, 347) * mm, "end": v(914.04, 327) * mm});
            skLineSegment(sketch, "E27", {"start": v(839.04, 347) * mm, "end": v(839.04, 327) * mm});
            skLineSegment(sketch, "E28", {"start": v(764.04, 347) * mm, "end": v(764.04, 327) * mm});
            skLineSegment(sketch, "E29", {"start": v(764.37, 277) * mm, "end": v(764.37, 257) * mm});
            skLineSegment(sketch, "E30", {"start": v(839.37, 277) * mm, "end": v(839.37, 257) * mm});
            skLineSegment(sketch, "E31", {"start": v(914.37, 277) * mm, "end": v(914.37, 257) * mm});
            skLineSegment(sketch, "E32", {"start": v(989.37, 277) * mm, "end": v(989.37, 257) * mm});
            skLineSegment(sketch, "E33", {"start": v(1064.37, 277) * mm, "end": v(1064.37, 257) * mm});
            skLineSegment(sketch, "E34", {"start": v(1139.37, 277) * mm, "end": v(1139.37, 257) * mm});
            skLineSegment(sketch, "E35", {"start": v(1214.37, 277) * mm, "end": v(1214.37, 257) * mm});
            skLineSegment(sketch, "E36", {"start": v(1289.37, 277) * mm, "end": v(1289.37, 257) * mm});
            skLineSegment(sketch, "E37", {"start": v(1289.7, 207) * mm, "end": v(1289.7, 187) * mm});
            skLineSegment(sketch, "E38", {"start": v(1214.7, 207) * mm, "end": v(1214.7, 187) * mm});
            skLineSegment(sketch, "E39", {"start": v(1139.7, 207) * mm, "end": v(1139.7, 187) * mm});
            skLineSegment(sketch, "E40", {"start": v(1064.7, 207) * mm, "end": v(1064.7, 187) * mm});
            skLineSegment(sketch, "E41", {"start": v(989.7, 207) * mm, "end": v(989.7, 187) * mm});
            skLineSegment(sketch, "E42", {"start": v(914.7, 207) * mm, "end": v(914.7, 187) * mm});
            skLineSegment(sketch, "E43", {"start": v(839.7, 207) * mm, "end": v(839.7, 187) * mm});
            skLineSegment(sketch, "E44", {"start": v(764.7, 207) * mm, "end": v(764.7, 187) * mm});
            skLineSegment(sketch, "E45", {"start": v(765.04, 137) * mm, "end": v(765.04, 117) * mm});
            skLineSegment(sketch, "E46", {"start": v(840.04, 137) * mm, "end": v(840.04, 117) * mm});
            skLineSegment(sketch, "E47", {"start": v(915.04, 137) * mm, "end": v(915.04, 117) * mm});
            skLineSegment(sketch, "E48", {"start": v(990.04, 137) * mm, "end": v(990.04, 117) * mm});
            skLineSegment(sketch, "E49", {"start": v(1065.04, 137) * mm, "end": v(1065.04, 117) * mm});
            skLineSegment(sketch, "E50", {"start": v(1140.04, 137) * mm, "end": v(1140.04, 117) * mm});
            skLineSegment(sketch, "E51", {"start": v(1215.04, 137) * mm, "end": v(1215.04, 117) * mm});
            skLineSegment(sketch, "E52", {"start": v(1290.04, 137) * mm, "end": v(1290.04, 117) * mm});
            skLineSegment(sketch, "E53", {"start": v(1290.37, 67) * mm, "end": v(1290.37, 47) * mm});
            skLineSegment(sketch, "E54", {"start": v(1215.37, 67) * mm, "end": v(1215.37, 47) * mm});
            skLineSegment(sketch, "E55", {"start": v(1140.37, 67) * mm, "end": v(1140.37, 47) * mm});
            skLineSegment(sketch, "E56", {"start": v(1065.37, 67) * mm, "end": v(1065.37, 47) * mm});
            skLineSegment(sketch, "E57", {"start": v(990.37, 67) * mm, "end": v(990.37, 47) * mm});
            skLineSegment(sketch, "E58", {"start": v(915.37, 67) * mm, "end": v(915.37, 47) * mm});
            skLineSegment(sketch, "E59", {"start": v(840.37, 67) * mm, "end": v(840.37, 47) * mm});
            skLineSegment(sketch, "E60", {"start": v(765.37, 67) * mm, "end": v(765.37, 47) * mm});
            skLineSegment(sketch, "E61", {"start": v(765.7, -3) * mm, "end": v(765.7, -23) * mm});
            skLineSegment(sketch, "E62", {"start": v(840.7, -3) * mm, "end": v(840.7, -23) * mm});
            skLineSegment(sketch, "E63", {"start": v(915.7, -3) * mm, "end": v(915.7, -23) * mm});
            skLineSegment(sketch, "E64", {"start": v(990.7, -3) * mm, "end": v(990.7, -23) * mm});
            skLineSegment(sketch, "E65", {"start": v(1065.7, -3) * mm, "end": v(1065.7, -23) * mm});
            skLineSegment(sketch, "E66", {"start": v(1140.7, -3) * mm, "end": v(1140.7, -23) * mm});
            skLineSegment(sketch, "E67", {"start": v(1215.7, -3) * mm, "end": v(1215.7, -23) * mm});
            skLineSegment(sketch, "E68", {"start": v(1290.7, -3) * mm, "end": v(1290.7, -23) * mm});
            skLineSegment(sketch, "E69", {"start": v(1291.03, -73) * mm, "end": v(1291.03, -93) * mm});
            skLineSegment(sketch, "E70", {"start": v(1216.03, -73) * mm, "end": v(1216.03, -93) * mm});
            skLineSegment(sketch, "E71", {"start": v(1141.03, -73) * mm, "end": v(1141.03, -93) * mm});
            skLineSegment(sketch, "E72", {"start": v(1066.03, -73) * mm, "end": v(1066.03, -93) * mm});
            skLineSegment(sketch, "E73", {"start": v(991.03, -73) * mm, "end": v(991.03, -93) * mm});
            skLineSegment(sketch, "E74", {"start": v(841.03, -73) * mm, "end": v(841.03, -93) * mm});
            skLineSegment(sketch, "E75", {"start": v(766.03, -73) * mm, "end": v(766.03, -93) * mm});
            skLineSegment(sketch, "E76", {"start": v(916.03, -73) * mm, "end": v(916.03, -93) * mm});
            skLineSegment(sketch, "E77.bottom", {"start": v(-286.5, -1052.3) * mm, "end": v(487.9, -1052.3) * mm});
            skLineSegment(sketch, "E77.top", {"start": v(-286.5, -1357.1) * mm, "end": v(487.9, -1357.1) * mm});
            skLineSegment(sketch, "E77.left", {"start": v(-286.5, -1052.3) * mm, "end": v(-286.5, -1357.1) * mm});
            skLineSegment(sketch, "E77.right", {"start": v(487.9, -1052.3) * mm, "end": v(487.9, -1357.1) * mm});
            skLineSegment(sketch, "E78", {"start": v(100.7, -1052.3) * mm, "end": v(100.7, -1357.1) * mm, "construction": true});
            skSolve(sketch);
        }
        {
            var Q0;
            Q0=makeQuery(id+"F9.imprint","IMPRINT",FACE,{"disambiguationData":[TD([[makeQuery(id+"F9.imprint","IMPRINT",EDGE,{"derivedFrom":sQuery(id+"F9.wireOp",EDGE,"E10.bottom")}),-1.0]])]});
            extrude(context, id + "F10", {"entities" : qUnion([Q0]), "depth" : 30 * mm});
        }
        {
            var Q0;
            Q0=makeQuery(id+"F9.imprint","IMPRINT",FACE,{"disambiguationData":[TD([[makeQuery(id+"F9.imprint","IMPRINT",EDGE,{"derivedFrom":sQuery(id+"F9.wireOp",EDGE,"E77.bottom")}),-1.0]])]});
            extrude(context, id + "F11", {"entities" : qUnion([Q0]), "depth" : 4.76 * mm});
        }
        {
            var Q0;
            Q0=makeQuery(id+"F9.imprint","IMPRINT",FACE,{"disambiguationData":[TD([[makeQuery(id+"F9.imprint","IMPRINT",EDGE,{"derivedFrom":sQuery(id+"F9.wireOp",EDGE,"E77.bottom")}),-1.0]])]});
            var sketch = newSketch(context, id + "F12", { "sketchPlane" : qUnion([Q0])});
            skLineSegment(sketch, "E79.bottom", {"start": v(-286.5, -1357.1) * mm, "end": v(487.9, -1357.1) * mm});
            skLineSegment(sketch, "E79.top", {"start": v(-286.5, -1361.87) * mm, "end": v(487.9, -1361.87) * mm});
            skLineSegment(sketch, "E79.left", {"start": v(-286.5, -1357.1) * mm, "end": v(-286.5, -1361.87) * mm});
            skLineSegment(sketch, "E79.right", {"start": v(487.9, -1357.1) * mm, "end": v(487.9, -1361.87) * mm});
            skSolve(sketch);
        }
        {
            var Q0;
            Q0=makeQuery(id+"F12.imprint","IMPRINT",FACE,{"disambiguationData":[TD([[makeQuery(id+"F12.imprint","IMPRINT",EDGE,{"derivedFrom":sQuery(id+"F12.wireOp",EDGE,"E79.bottom")}),-1.0]])]});
            extrude(context, id + "F13", {"entities" : qUnion([Q0]), "operationType" : NewBodyOperationType.ADD, "depth" : 20 * mm});
        }
        {
            var Q0;
            Q0=makeQuery(id+"F13.boolean.opBoolean","MERGE",FACE,{"derivedFrom":[makeQuery(id+"F11.opExtrude","SWEPT_FACE",FACE,{"disambiguationData":[OSD([sQuery(id+"F9.wireOp",EDGE,"E77.left")])]}),makeQuery(id+"F13.opExtrude","SWEPT_FACE",FACE,{"disambiguationData":[OSD([sQuery(id+"F12.wireOp",EDGE,"E79.left")])]})]});
            var sketch = newSketch(context, id + "F14", { "sketchPlane" : qUnion([Q0])});
            skLineSegment(sketch, "E80", {"start": v(0, -1052.3) * mm, "end": v(-23.7, -1058.22) * mm});
            skLineSegment(sketch, "E81", {"start": v(-23.7, -1058.22) * mm, "end": v(0, -1153.3) * mm});
            skSolve(sketch);
        }
        {
            var Q0;
            {var subQ0=sQuery(id+"F14.wireOp",EDGE,"E80");Q0=makeQuery(id+"F14.imprint","IMPRINT",FACE,{"disambiguationData":[TD([[makeQuery(id+"F14.imprint","IMPRINT",EDGE,{"derivedFrom":subQ0}),1.0]])]});}
            extrude(context, id + "F15", {"entities" : qUnion([Q0]), "operationType" : NewBodyOperationType.ADD, "oppositeDirection" : true, "depth" : 4 * mm});
        }
        {
            var Q0;
            Q0=makeQuery(id+"F13.boolean.opBoolean","MERGE",FACE,{"derivedFrom":[makeQuery(id+"F11.opExtrude","SWEPT_FACE",FACE,{"disambiguationData":[OSD([sQuery(id+"F9.wireOp",EDGE,"E77.right")])]}),makeQuery(id+"F13.opExtrude","SWEPT_FACE",FACE,{"disambiguationData":[OSD([sQuery(id+"F12.wireOp",EDGE,"E79.right")])]})]});
            var sketch = newSketch(context, id + "F16", { "sketchPlane" : qUnion([Q0])});
            skLineSegment(sketch, "E82", {"start": v(0, -1052.3) * mm, "end": v(23.7, -1058.22) * mm});
            skLineSegment(sketch, "E83", {"start": v(23.7, -1058.22) * mm, "end": v(0, -1153.3) * mm});
            skSolve(sketch);
        }
        {
            var Q0;
            {var subQ0=sQuery(id+"F16.wireOp",EDGE,"E82");Q0=makeQuery(id+"F16.imprint","IMPRINT",FACE,{"disambiguationData":[TD([[makeQuery(id+"F16.imprint","IMPRINT",EDGE,{"derivedFrom":subQ0}),-1.0]])]});}
            extrude(context, id + "F17", {"entities" : qUnion([Q0]), "operationType" : NewBodyOperationType.ADD, "oppositeDirection" : true, "depth" : 4.76 * mm});
        }
        {
            var Q0;
            Q0=qCreatedBy(makeId("Front.planeOp"),FACE);
            var sketch = newSketch(context, id + "F18", { "sketchPlane" : qUnion([Q0])});
            skLineSegment(sketch, "E84.bottom", {"start": v(-449.42, 805.88) * mm, "end": v(464.98, 805.88) * mm});
            skLineSegment(sketch, "E84.top", {"start": v(-449.42, 348.68) * mm, "end": v(464.98, 348.68) * mm});
            skLineSegment(sketch, "E84.left", {"start": v(-449.42, 805.88) * mm, "end": v(-449.42, 348.68) * mm});
            skLineSegment(sketch, "E84.right", {"start": v(464.98, 805.88) * mm, "end": v(464.98, 348.68) * mm});
            skSolve(sketch);
        }
        {
            var Q0;
            Q0=makeQuery(id+"F18.imprint","IMPRINT",FACE,{"disambiguationData":[TD([[makeQuery(id+"F18.imprint","IMPRINT",EDGE,{"derivedFrom":sQuery(id+"F18.wireOp",EDGE,"E84.bottom")}),-1.0]])]});
            extrude(context, id + "F19", {"entities" : qUnion([Q0]), "depth" : 5 * mm});
        }
        {
            var Q0;
            Q0=qCreatedBy(makeId("Front.planeOp"),FACE);
            var sketch = newSketch(context, id + "F20", { "sketchPlane" : qUnion([Q0])});
            skLineSegment(sketch, "E85.bottom", {"start": v(243.65, -278.52) * mm, "end": v(540.65, -278.52) * mm});
            skLineSegment(sketch, "E85.top", {"start": v(243.65, -488.52) * mm, "end": v(540.65, -488.52) * mm});
            skLineSegment(sketch, "E85.left", {"start": v(243.65, -278.52) * mm, "end": v(243.65, -488.52) * mm});
            skLineSegment(sketch, "E85.right", {"start": v(540.65, -278.52) * mm, "end": v(540.65, -488.52) * mm});
            skSolve(sketch);
        }
        {
            var Q0;
            Q0=makeQuery(id+"F20.imprint","IMPRINT",FACE,{"disambiguationData":[TD([[makeQuery(id+"F20.imprint","IMPRINT",EDGE,{"derivedFrom":sQuery(id+"F20.wireOp",EDGE,"E85.bottom")}),-1.0]])]});
            extrude(context, id + "F21", {"entities" : qUnion([Q0]), "depth" : 1 * mm});
        }
    });
